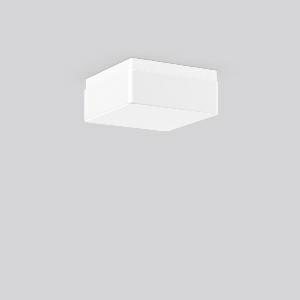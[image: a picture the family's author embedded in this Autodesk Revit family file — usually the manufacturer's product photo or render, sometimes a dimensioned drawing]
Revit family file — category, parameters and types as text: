
# Revit family: quadrat_201412_002_1_ef54
name_source: partatom
category: Lighting Fixtures
units: mm (PartAtom-declared; Revit-internal decimal feet)

## family parameters
Cut with Voids When Loaded = No
Host = Face
Light Source = No
Part Type = Normal
Room Calculation Point = No
Round Connector Dimension = Use Diameter
Shared = No

## types (1)
- QUADRAT (1 x LED Modul 840, 1100 lm, 4000)
    Apparent Load = 11 VA
    CIE Flux Codes = 38 67 88 80 100
    Color Rendering = 80
    Color Temperature = 4000
    Default Elevation = 1800 mm
    Description = Series: QUADRAT
Square surface-mounted luminaire in classic design. Base: plastic. Opal glass: mouth blown, silk finish. Diffuser fastening: spring system. Suitable for Ceiling mounting, Wall (surface). IP 43 ceiling mounting, IP 44 wall mounting. 
Colour: white
Length: 280 mm
Width: 280 mm
Height: 120 mm
Lamp: LED exchangeable
Socket: without socket
Colour temperature: 4000K
Colour rendering index (CRI): 80
System power: 11 W
Rated luminous flux: 1100 lm
Luminous efficiency: 100 lm/W
Control gear: AC Strom, dim.Ph.an-/abschnitt
Protection class: I
Type of protection: IP 43
    Height = 120 mm
    Lamp = 1 x LED Modul 840
    Lamp Light Flux = 1100 lm
    Lamp count = 1
    Length = 280 mm
    Lifetime = 50000 h
    Luminous efficacy = 100 lm/W
    Manufacturer = RZB
    ModVariant = No
    Model = 201412.002.1
    Mounting Place = Ceiling, Wall
    Mounting Type = Surface mounted
    Number of Poles = 1
    OnlyDefault = Yes
    Power Factor = 1
    Product Name = QUADRAT
    Product group = Surface mounted ceiling and wall luminaires
    ProductGroupID = 305
    Protection Class = Protection class I
    Protection Degree = IP 43
    RLX_Detail_Level = 1
    RLX_Emergency_Light_Flux = 0 lm
    RLX_Emergency_Type = 0
    RLX_Emergency_Type_DB = No
    RlxData = <blob elided: 11509 chars, md5=b9d1f8ef>
    Socket = socket
    Standby Power = 0 W
    System Light Flux = 1100 lm
    System Power = 11 W
    Type Comments = Product without accessories
    Type Image = 20129.002.jpg
    URL = http://relux.com
    VarID = ---
    Voltage = 230 V
    Voltage Range = 220-240 V
    Weight = 0.00 kg
    Width = 280 mm

## geometry (parser evidence)
native form markers: Sweep x11
no freeform markers — native parametric forms only
